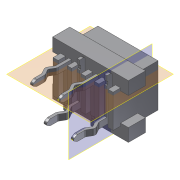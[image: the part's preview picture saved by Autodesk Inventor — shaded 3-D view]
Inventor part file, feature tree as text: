
AUTODESK INVENTOR PART (.ipt)
format: ipt  version: 2014 (Build 180170000, 170)  size: 510,976 bytes
history: native  units: mm
features: other x3, plane x2
ambient origin geometry x8: Origin, YZ Plane, XZ Plane, XY Plane, X Axis, Y Axis, Z Axis, Center Point
bodies: Volumenkörper1 (feature_tree)
feature tree (5):
  other  "micro-miniature_steckverbinder_a-32-04v-130x0"
  other  "Arbeitspunkt1"
  other  "Arbeitspunkt2"
  plane  "Arbeitsebene1"
  plane  "Arbeitsebene2"
